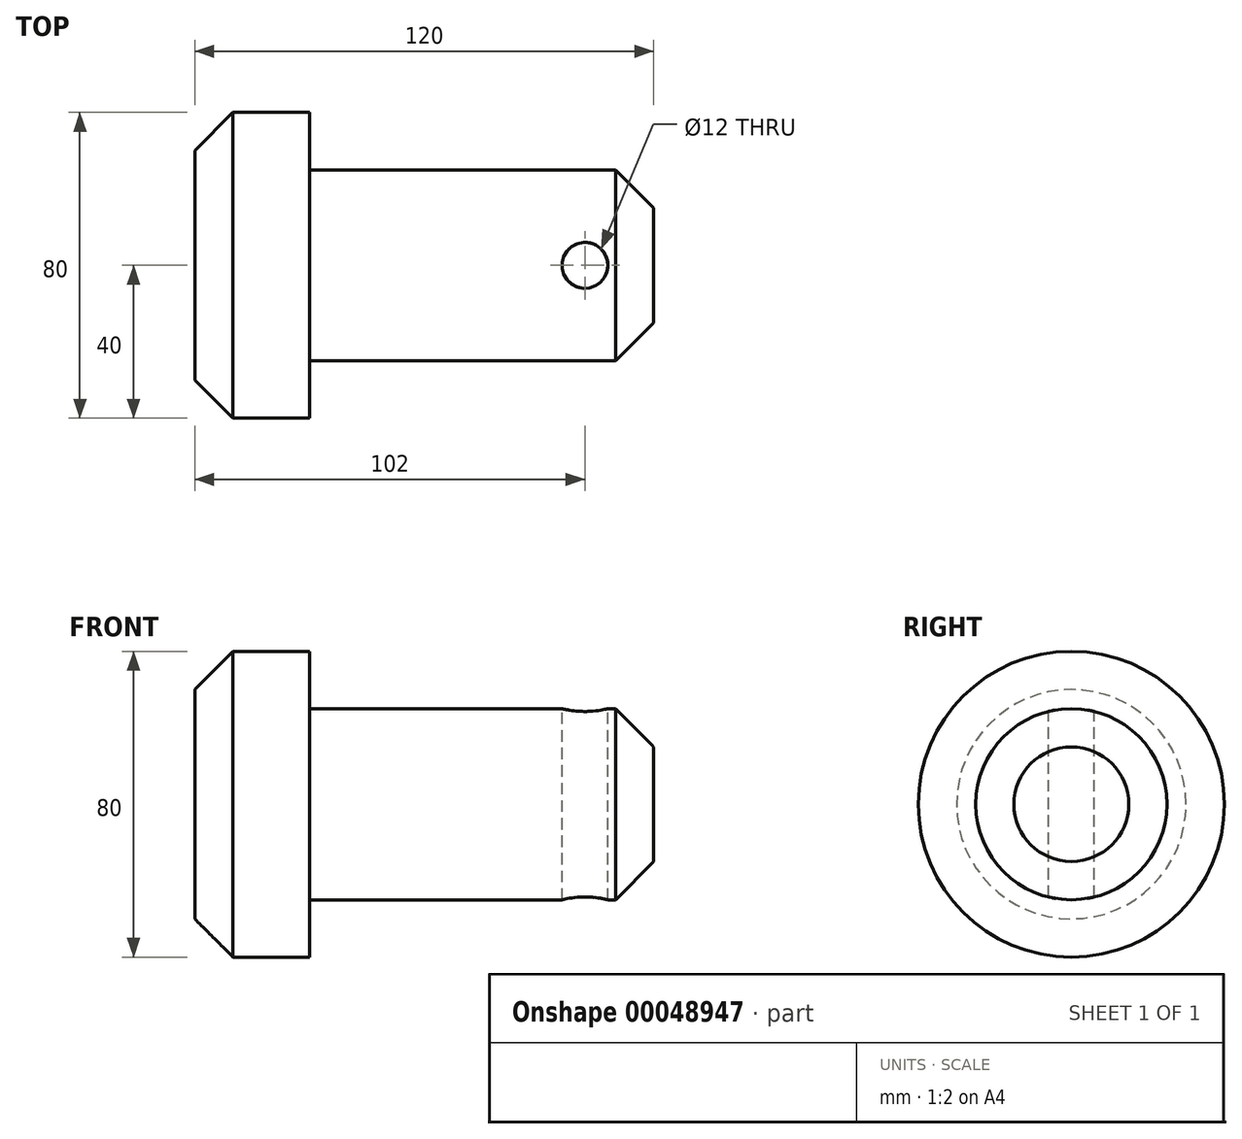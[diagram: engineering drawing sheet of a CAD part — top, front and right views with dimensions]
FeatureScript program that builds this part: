
annotation { "Feature Type Name" : "Feature", "Feature Type Description" : "" }
export const myFeature = defineFeature(function(context is Context, id is Id, definition is map)
    precondition{}
    {
        {
            var Q0;
            Q0=qCreatedBy(makeId("Front.planeOp"),FACE);
            var sketch = newSketch(context, id + "F0", { "sketchPlane" : qUnion([Q0])});
            skLineSegment(sketch, "E0", {"start": v(0, 0) * mm, "end": v(0, 40) * mm});
            skLineSegment(sketch, "E1", {"start": v(0, 40) * mm, "end": v(30, 40) * mm});
            skLineSegment(sketch, "E2", {"start": v(30, 40) * mm, "end": v(30, 25) * mm});
            skLineSegment(sketch, "E3", {"start": v(30, 25) * mm, "end": v(120, 25) * mm});
            skLineSegment(sketch, "E4", {"start": v(120, 25) * mm, "end": v(120, 0) * mm});
            skLineSegment(sketch, "E5", {"start": v(120, 0) * mm, "end": v(0, 0) * mm});
            skSolve(sketch);
        }
        {
            var Q0;
            Q0=makeQuery(id+"F0.imprint","IMPRINT",FACE,{"disambiguationData":[TD([[makeQuery(id+"F0.imprint","IMPRINT",EDGE,{"derivedFrom":sQuery(id+"F0.wireOp",EDGE,"E0")}),-1.0]])]});
            var Q1;
            Q1=sQuery(id+"F0.wireOp",EDGE,"E5");
            revolve(context, id + "F1", {"entities" : qUnion([Q0]), "axis" : qUnion([Q1]), "revolveType" : RevolveType.FULL});
        }
        {
            var Q0;
            Q0=makeQuery(id+"F1.opRevolve","SWEPT_EDGE",EDGE,{"disambiguationData":[OSD([sQuery(id+"F0.wireOp",EDGE,"E0"),sQuery(id+"F0.wireOp",EDGE,"E1")])]});
            chamfer(context, id + "F2", {"entities" : qUnion([Q0]), "chamferType" : ChamferType.OFFSET_ANGLE, "width" : 10 * mm, "oppositeDirection" : false, "angle" : 45 * degree, "tangentPropagation" : true});
        }
        {
            var Q0;
            Q0=makeQuery(id+"F1.opRevolve","SWEPT_EDGE",EDGE,{"disambiguationData":[OSD([sQuery(id+"F0.wireOp",EDGE,"E3"),sQuery(id+"F0.wireOp",EDGE,"E4")])]});
            chamfer(context, id + "F3", {"entities" : qUnion([Q0]), "chamferType" : ChamferType.OFFSET_ANGLE, "width" : 10 * mm, "oppositeDirection" : false, "angle" : 45 * degree, "tangentPropagation" : true});
        }
        {
            var Q0;
            Q0=qCreatedBy(makeId("Top.planeOp"),FACE);
            var sketch = newSketch(context, id + "F4", { "sketchPlane" : qUnion([Q0])});
            skLineSegment(sketch, "E6", {"start": v(102, 0) * mm, "end": v(30, 0) * mm});
            skLineSegment(sketch, "E7", {"start": v(30, 0) * mm, "end": v(30, -79.3) * mm, "construction": true});
            skLineSegment(sketch, "E8", {"start": v(0, 0) * mm, "end": v(152.18, 0) * mm, "construction": true});
            skLineSegment(sketch, "E9", {"start": v(102, 0) * mm, "end": v(102, 0) * mm});
            skCircle(sketch, "E10", {"center": v(102, 0) * mm, "radius": 6 * mm});
            skSolve(sketch);
        }
        {
            var Q0;
            Q0 = qSketchRegion(id + "F4", true);
            extrude(context, id + "F5", {"entities" : qUnion([Q0]), "operationType" : NewBodyOperationType.REMOVE, "endBound" : BoundingType.THROUGH_ALL, "oppositeDirection" : true, "depth" : 25 * mm, "hasSecondDirection" : true, "secondDirectionBound" : SecondDirectionBoundingType.THROUGH_ALL, "secondDirectionOppositeDirection" : false, "secondDirectionDepth" : 25 * mm});
        }
    });
